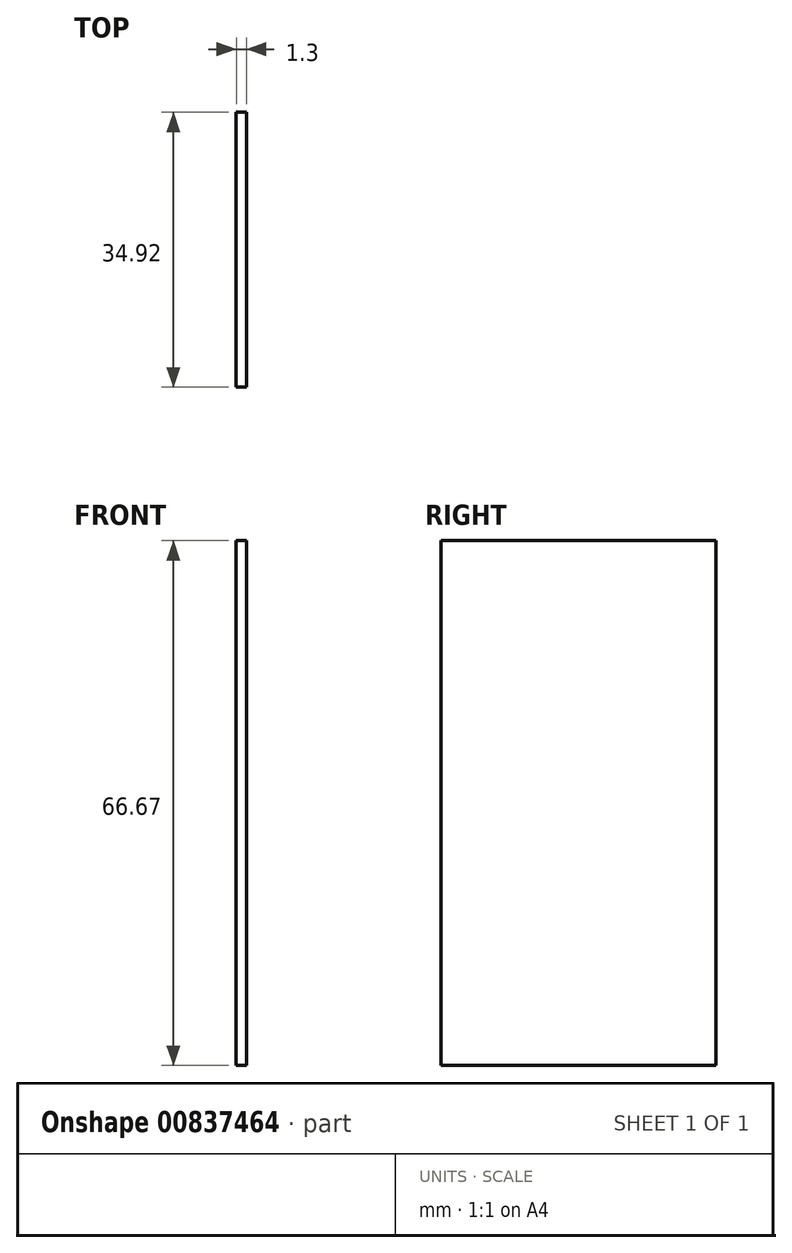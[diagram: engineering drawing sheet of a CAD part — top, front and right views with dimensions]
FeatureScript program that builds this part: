
annotation { "Feature Type Name" : "Feature", "Feature Type Description" : "" }
export const myFeature = defineFeature(function(context is Context, id is Id, definition is map)
    precondition{}
    {
        {
            var Q0;
            Q0=qCreatedBy(makeId("Right.planeOp"),FACE);
            var sketch = newSketch(context, id + "F0", { "sketchPlane" : qUnion([Q0])});
            skLineSegment(sketch, "E0.bottom", {"start": v(0, 0) * mm, "end": v(34.93, 0) * mm});
            skLineSegment(sketch, "E0.top", {"start": v(0, 66.68) * mm, "end": v(34.92, 66.68) * mm});
            skLineSegment(sketch, "E0.left", {"start": v(0, 0) * mm, "end": v(0, 66.68) * mm});
            skLineSegment(sketch, "E0.right", {"start": v(34.93, 0) * mm, "end": v(34.92, 66.68) * mm});
            skSolve(sketch);
        }
        {
            var Q0;
            Q0=makeQuery(id+"F0.imprint","IMPRINT",FACE,{"disambiguationData":[TD([[makeQuery(id+"F0.imprint","IMPRINT",EDGE,{"derivedFrom":sQuery(id+"F0.wireOp",EDGE,"E0.bottom")}),1.0]])]});
            extrude(context, id + "F1", {"entities" : qUnion([Q0]), "endBound" : BoundingType.SYMMETRIC, "depth" : (66 + 3 / 8) / 50.8 * mm, "offsetDistance" : 25.4 * mm});
        }
    });
